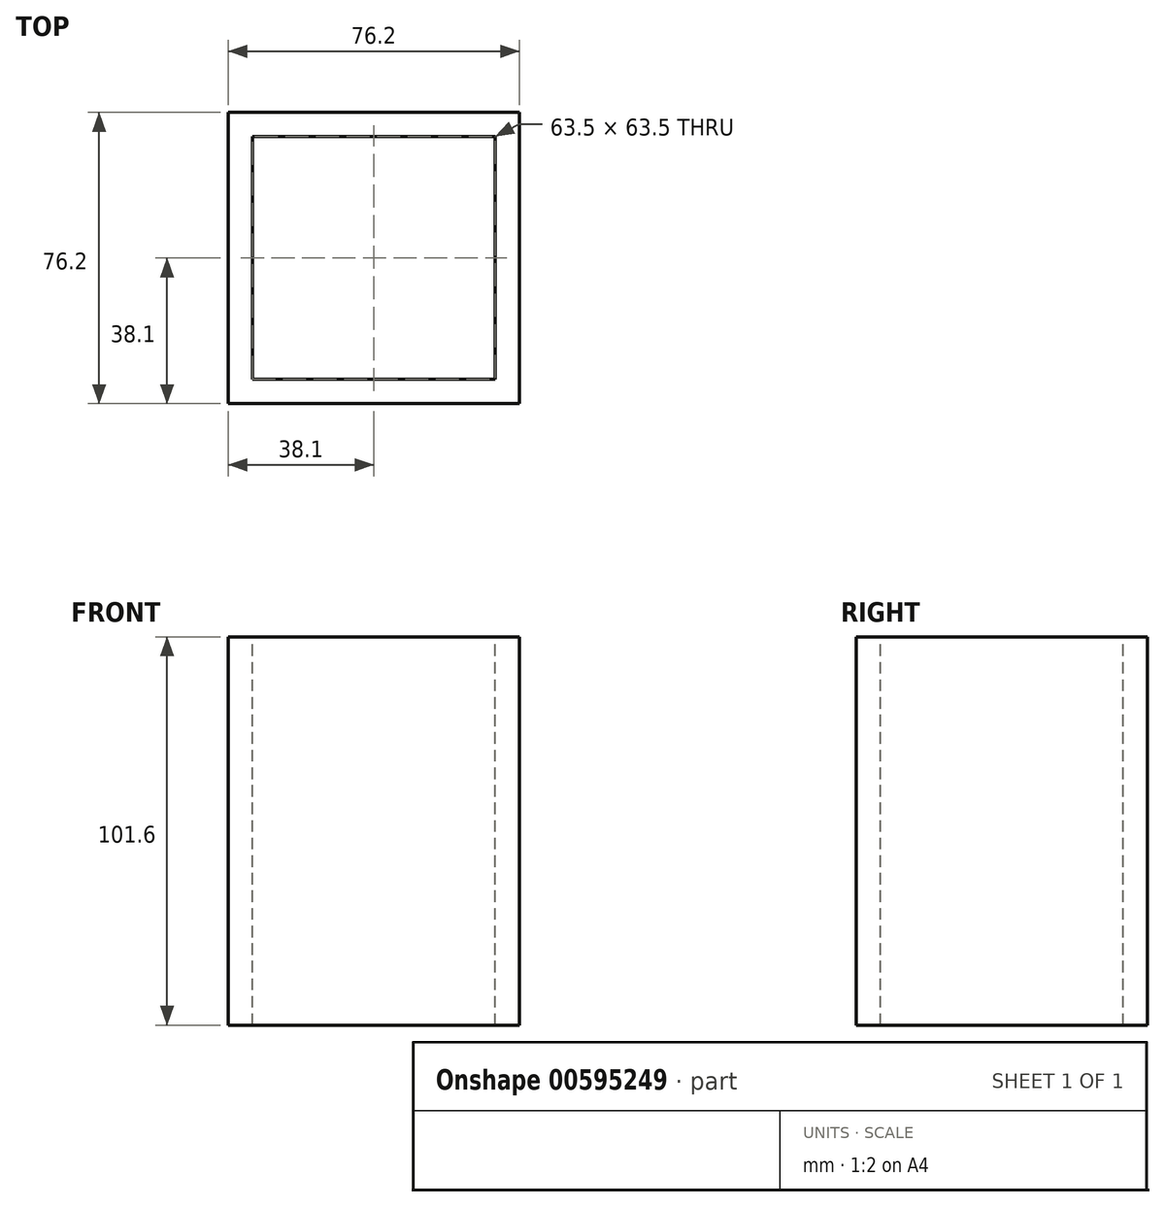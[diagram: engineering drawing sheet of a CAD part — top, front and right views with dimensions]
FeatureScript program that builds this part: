
annotation { "Feature Type Name" : "Feature", "Feature Type Description" : "" }
export const myFeature = defineFeature(function(context is Context, id is Id, definition is map)
    precondition{}
    {
        {
            var Q0;
            Q0=qCreatedBy(makeId("Front.planeOp"),FACE);
            var sketch = newSketch(context, id + "F0", { "sketchPlane" : qUnion([Q0])});
            skLineSegment(sketch, "E0.bottom", {"start": v(38.1, -50.8) * mm, "end": v(-38.1, -50.8) * mm});
            skLineSegment(sketch, "E0.top", {"start": v(38.1, 50.8) * mm, "end": v(-38.1, 50.8) * mm});
            skLineSegment(sketch, "E0.left", {"start": v(38.1, -50.8) * mm, "end": v(38.1, 50.8) * mm});
            skLineSegment(sketch, "E0.right", {"start": v(-38.1, -50.8) * mm, "end": v(-38.1, 50.8) * mm});
            skPoint(sketch, "E0.middle", {"position": v(0, 0) * mm});
            skSolve(sketch);
        }
        {
            var Q0;
            Q0=makeQuery(id+"F0.imprint","IMPRINT",FACE,{"disambiguationData":[TD([[makeQuery(id+"F0.imprint","IMPRINT",EDGE,{"derivedFrom":sQuery(id+"F0.wireOp",EDGE,"E0.bottom")}),-1.0]])]});
            extrude(context, id + "F1", {"entities" : qUnion([Q0]), "depth" : 76.2 * mm, "offsetDistance" : 25.4 * mm});
        }
        {
            var Q0;
            Q0=makeQuery(id+"F1.opExtrude","SWEPT_FACE",FACE,{"disambiguationData":[OSD([sQuery(id+"F0.wireOp",EDGE,"E0.top")])]});
            var sketch = newSketch(context, id + "F2", { "sketchPlane" : qUnion([Q0])});
            skLineSegment(sketch, "E1.bottom", {"start": v(31.75, -69.85) * mm, "end": v(-31.75, -69.85) * mm});
            skLineSegment(sketch, "E1.top", {"start": v(31.75, -6.35) * mm, "end": v(-31.75, -6.35) * mm});
            skLineSegment(sketch, "E1.left", {"start": v(31.75, -69.85) * mm, "end": v(31.75, -6.35) * mm});
            skLineSegment(sketch, "E1.right", {"start": v(-31.75, -69.85) * mm, "end": v(-31.75, -6.35) * mm});
            skPoint(sketch, "E1.middle", {"position": v(0, -38.1) * mm});
            skPoint(sketch, "E1.middle.positionSnap0", {"position": v(38.1, -38.1) * mm});
            skPoint(sketch, "E1.centerSnap0", {"position": v(38.1, -38.1) * mm});
            skSolve(sketch);
        }
        {
            var Q0;
            Q0=makeQuery(id+"F2.imprint","IMPRINT",FACE,{"disambiguationData":[TD([[makeQuery(id+"F2.imprint","IMPRINT",EDGE,{"derivedFrom":sQuery(id+"F2.wireOp",EDGE,"E1.bottom")}),-1.0]])]});
            extrude(context, id + "F3", {"entities" : qUnion([Q0]), "operationType" : NewBodyOperationType.REMOVE, "oppositeDirection" : true, "depth" : 101.6 * mm, "offsetDistance" : 25.4 * mm});
        }
    });
